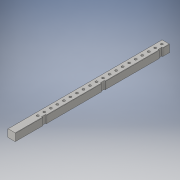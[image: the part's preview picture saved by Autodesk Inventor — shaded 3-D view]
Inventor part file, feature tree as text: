
AUTODESK INVENTOR PART (.ipt)
format: ipt  version: 2016 (Build 200138000, 138)  size: 214,016 bytes
history: native  units: in
note: dims shown in document units (in); Inventor stores cm internally (conversion verified against a paired STEP export)
features: extrude x3, sketch x3, chamfer x1, fillet x1
ambient origin geometry x8: Origin, YZ Plane, XZ Plane, XY Plane, X Axis, Y Axis, Z Axis, Center Point
bodies: Solid1 (feature_tree)
feature tree (8):
  extrude  "4x4 Stock"  Depth=3.5in
  extrude  "Center Support Slots"  Depth=12.5in
  extrude  "Extrusion3"  TaperAngle=180.0deg  [1 undecoded]
  chamfer  "Chamfer1"  Distance=1.75in
  fillet  "Fillet1"  Radius=39.5in
  sketch  "Sketch1"  dims[d0=3.5in d1=3.5in]
  sketch  "Sketch2"  dims[d2=72.0in d3=0.0in d4=12.5in]
  sketch  "Sketch3"  dims[d5=0.5in d6=180.0deg d7=1.75in d8=39.5in d9=0.5in d10=1.75in d11=66.0in d12=0.5in d13=1.75in d14=4.0in d15=0.0in d16=12.0in d17=3.0in d18=3.0in d19=3.0in d20=3.0in d21=3.0in d22=3.0in d23=3.0in d24=3.0in d25=3.0in d26=3.0in d27=3.0in d28=3.0in d29=3.0in d30=3.0in d31=3.0in d32=3.0in d33=3.0in d34=3.0in d35=3.0in d36=1.0in d37=1.0in d38=1.0in d39=1.0in d40=1.0in d41=1.0in d42=1.0in d43=1.0in d44=1.0in d45=1.0in d46=1.0in d47=1.0in d48=1.0in d49=1.0in d50=1.0in d51=1.0in d52=1.0in d53=1.0in d54=1.0in d55=1.0in d56=4.0in d57=0.0in d58=1.25in d59=0.125in d60=45.0deg d61=0.125in]
note: 1 required parameter value undecoded (feature->parameter linkage not recoverable at this tier; creation-order binding heuristic only, values carry confidence <= 0.55)
